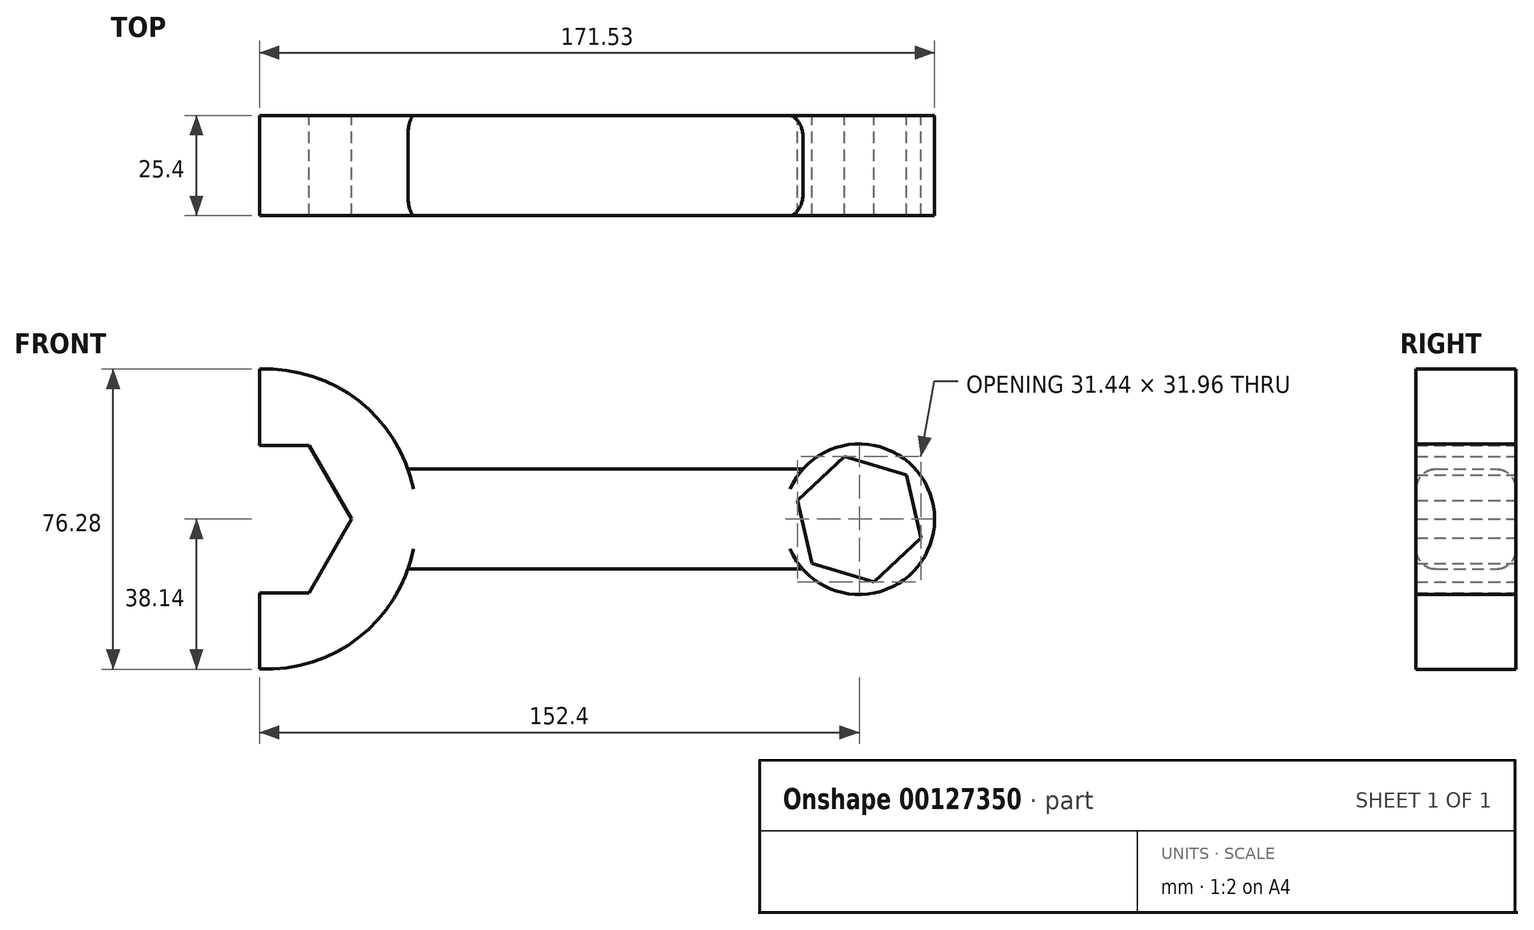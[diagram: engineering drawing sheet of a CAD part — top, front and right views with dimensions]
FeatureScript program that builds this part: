
annotation { "Feature Type Name" : "Feature", "Feature Type Description" : "" }
export const myFeature = defineFeature(function(context is Context, id is Id, definition is map)
    precondition{}
    {
        {
            var Q0;
            Q0=qCreatedBy(makeId("Front.planeOp"),FACE);
            var sketch = newSketch(context, id + "F0", { "sketchPlane" : qUnion([Q0])});
            skLineSegment(sketch, "E0.top", {"start": v(61.9, -12.7) * mm, "end": v(-38.44, -12.7) * mm});
            skPoint(sketch, "E0.middle", {"position": v(0, 0) * mm});
            skArc(sketch, "E1", {"start": v(-76.2, -38.1) * mm, "mid": v(-53.11, -31.65) * mm, "end": v(-38.44, -12.7) * mm});
            skPoint(sketch, "E0.right.start.orphan", {"position": v(-76.2, 12.7) * mm});
            skPoint(sketch, "E2.orphan", {"position": v(-76.2, -12.7) * mm});
            skArc(sketch, "E3.trimOffspring", {"start": v(-38.44, 12.7) * mm, "mid": v(-53.11, 31.65) * mm, "end": v(-76.2, 38.1) * mm});
            skCircle(sketch, "E4", {"center": v(76.2, 0) * mm, "radius": 19.13 * mm});
            skPoint(sketch, "E5.orphan", {"position": v(76.2, -12.7) * mm});
            skLineSegment(sketch, "E6.trimOffspring", {"start": v(61.9, 12.7) * mm, "end": v(-38.44, 12.7) * mm});
            skPoint(sketch, "E0.bottom.start.orphan", {"position": v(76.2, 12.7) * mm});
            skLineSegment(sketch, "E7.0", {"start": v(88.16, 11.24) * mm, "end": v(91.92, -4.74) * mm});
            skLineSegment(sketch, "E7.1", {"start": v(91.92, -4.74) * mm, "end": v(79.96, -15.98) * mm});
            skLineSegment(sketch, "E7.2", {"start": v(79.96, -15.98) * mm, "end": v(64.24, -11.24) * mm});
            skLineSegment(sketch, "E7.3", {"start": v(64.24, -11.24) * mm, "end": v(60.48, 4.74) * mm});
            skLineSegment(sketch, "E7.4", {"start": v(60.48, 4.74) * mm, "end": v(72.44, 15.98) * mm});
            skLineSegment(sketch, "E7.5", {"start": v(72.44, 15.98) * mm, "end": v(88.16, 11.24) * mm});
            skLineSegment(sketch, "E8.0", {"start": v(-52.72, 0) * mm, "end": v(-63.56, -18.78) * mm});
            skLineSegment(sketch, "E8.1", {"start": v(-63.56, -18.78) * mm, "end": v(-76.2, -18.78) * mm});
            skLineSegment(sketch, "E8.4", {"start": v(-76.2, 18.78) * mm, "end": v(-63.56, 18.78) * mm});
            skLineSegment(sketch, "E8.5", {"start": v(-63.56, 18.78) * mm, "end": v(-52.72, 0) * mm});
            skLineSegment(sketch, "E9", {"start": v(-52.72, 0) * mm, "end": v(-63.56, 18.78) * mm});
            skPoint(sketch, "E10.orphan", {"position": v(-85.25, 18.78) * mm});
            skPoint(sketch, "E11.start.orphan", {"position": v(-63.4, 22.73) * mm});
            skPoint(sketch, "E12.start.orphan", {"position": v(-63.4, -22.73) * mm});
            skPoint(sketch, "E13.start.orphan", {"position": v(-76.2, 25.4) * mm});
            skPoint(sketch, "E14.start.orphan", {"position": v(-76.2, -25.4) * mm});
            skLineSegment(sketch, "E15", {"start": v(-76.2, 38.1) * mm, "end": v(-76.2, 18.78) * mm});
            skLineSegment(sketch, "E16", {"start": v(-76.2, -38.1) * mm, "end": v(-76.2, -18.78) * mm});
            skLineSegment(sketch, "E17", {"start": v(72.44, 15.98) * mm, "end": v(60.48, 4.74) * mm});
            skLineSegment(sketch, "E18", {"start": v(64.24, -11.24) * mm, "end": v(79.96, -15.98) * mm});
            skLineSegment(sketch, "E19", {"start": v(91.92, -4.74) * mm, "end": v(88.16, 11.24) * mm});
            skSolve(sketch);
        }
        {
            var Q0;
            Q0 = qSketchRegion(id + "F0", true);
            extrude(context, id + "F1", {"entities" : qUnion([Q0]), "depth" : 25.4 * mm});
        }
        {
            var Q0;
            Q0=makeQuery(id+"F1.opExtrude","CAP_EDGE",EDGE,{"disambiguationData":[OSD([sQuery(id+"F0.wireOp",EDGE,"E0.top")])],"isStart":false});
            var Q1;
            Q1=makeQuery(id+"F1.opExtrude","CAP_EDGE",EDGE,{"disambiguationData":[OSD([sQuery(id+"F0.wireOp",EDGE,"E0.top")])],"isStart":true});
            var Q2;
            Q2=makeQuery(id+"F1.opExtrude","CAP_EDGE",EDGE,{"disambiguationData":[OSD([sQuery(id+"F0.wireOp",EDGE,"E6.trimOffspring")])],"isStart":true});
            var Q3;
            Q3=makeQuery(id+"F1.opExtrude","CAP_EDGE",EDGE,{"disambiguationData":[OSD([sQuery(id+"F0.wireOp",EDGE,"E6.trimOffspring")])],"isStart":false});
            fillet(context, id + "F2", {"entities" : qUnion([Q0, Q1, Q2, Q3]), "radius" : 5.08 * mm, "tangentPropagation" : true, "allowEdgeOverflow" : false});
        }
    });
